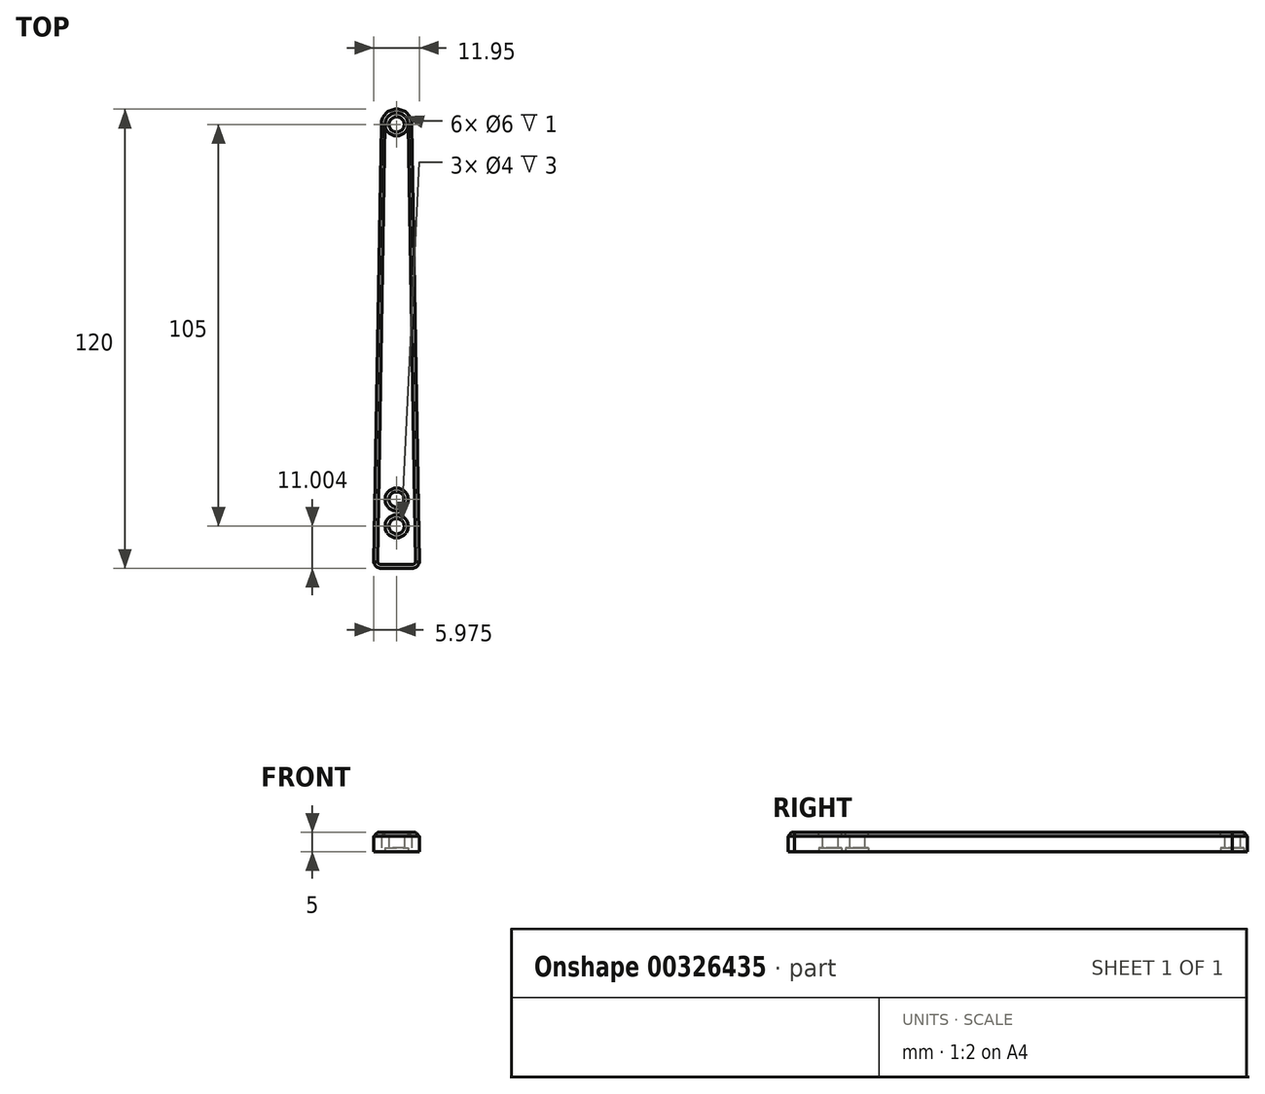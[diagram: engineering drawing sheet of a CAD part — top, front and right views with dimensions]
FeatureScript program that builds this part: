
annotation { "Feature Type Name" : "Feature", "Feature Type Description" : "" }
export const myFeature = defineFeature(function(context is Context, id is Id, definition is map)
    precondition{}
    {
        {
            var Q0;
            Q0=qCreatedBy(makeId("Top.planeOp"),FACE);
            var sketch = newSketch(context, id + "F0", { "sketchPlane" : qUnion([Q0])});
            skLineSegment(sketch, "E0.top", {"start": v(-57.1, -56.14) * mm, "end": v(-49.1, -56.14) * mm});
            skPoint(sketch, "E1", {"position": v(-53.1, 59.86) * mm});
            skArc(sketch, "E2", {"start": v(-49.1, 59.86) * mm, "mid": v(-53.1, 63.86) * mm, "end": v(-57.1, 59.86) * mm});
            skPoint(sketch, "E3.orphan", {"position": v(-57.1, 63.86) * mm});
            skPoint(sketch, "E0.bottom.end.orphan", {"position": v(-49.1, 63.86) * mm});
            skLineSegment(sketch, "E4", {"start": v(-57.1, 59.86) * mm, "end": v(-57.2, 54.18) * mm});
            skLineSegment(sketch, "E5", {"start": v(-49.1, 59.86) * mm, "end": v(-49, 54.18) * mm});
            skCircle(sketch, "E6", {"center": v(-53.1, 59.86) * mm, "radius": 2 * mm});
            skLineSegment(sketch, "E7", {"start": v(-53.1, 63.86) * mm, "end": v(-53.1, -56.14) * mm, "construction": true});
            skPoint(sketch, "E8", {"position": v(-53.1, -31.14) * mm});
            skPoint(sketch, "E9", {"position": v(-53.1, -36.14) * mm});
            skPoint(sketch, "E10", {"position": v(-53.1, -38.14) * mm});
            skPoint(sketch, "E11", {"position": v(-53.1, -45.14) * mm});
            skCircle(sketch, "E12", {"center": v(-53.1, -38.14) * mm, "radius": 2 * mm});
            skCircle(sketch, "E13", {"center": v(-53.1, -45.14) * mm, "radius": 2 * mm});
            skArc(sketch, "E14", {"start": v(-57.1, -56.14) * mm, "mid": v(-58.38, -55.66) * mm, "end": v(-59.07, -54.47) * mm});
            skArc(sketch, "E15", {"start": v(-49.1, -56.14) * mm, "mid": v(-47.8, -55.66) * mm, "end": v(-47.12, -54.47) * mm});
            skPoint(sketch, "E16.trimOffspring.end.orphan", {"position": v(-59.1, -56.14) * mm});
            skPoint(sketch, "E17.orphan", {"position": v(-47.1, -56.14) * mm});
            skLineSegment(sketch, "E18.trimOffspring", {"start": v(-57.29, 48.76) * mm, "end": v(-59.07, -54.47) * mm});
            skLineSegment(sketch, "E19.trimOffspring", {"start": v(-48.9, 48.76) * mm, "end": v(-47.12, -54.47) * mm});
            skLineSegment(sketch, "E20", {"start": v(-57.2, 54.18) * mm, "end": v(-57.22, 52.52) * mm});
            skLineSegment(sketch, "E21", {"start": v(-49, 54.18) * mm, "end": v(-48.97, 52.52) * mm});
            skLineSegment(sketch, "E22", {"start": v(-57.27, 49.52) * mm, "end": v(-57.29, 48.76) * mm});
            skLineSegment(sketch, "E23.trimOffspring", {"start": v(-48.92, 49.52) * mm, "end": v(-48.9, 48.76) * mm});
            skLineSegment(sketch, "E24", {"start": v(-48.97, 52.52) * mm, "end": v(-48.92, 49.52) * mm});
            skLineSegment(sketch, "E25", {"start": v(-57.22, 52.52) * mm, "end": v(-57.27, 49.52) * mm});
            skSolve(sketch);
        }
        {
            var Q0;
            Q0=makeQuery(id+"F0.imprint","IMPRINT",FACE,{"disambiguationData":[TD([[makeQuery(id+"F0.imprint","IMPRINT",EDGE,{"derivedFrom":sQuery(id+"F0.wireOp",EDGE,"E0.top")}),1.0]])]});
            extrude(context, id + "F1", {"entities" : qUnion([Q0]), "depth" : 5 * mm});
        }
        {
            var Q0;
            Q0=makeQuery(id+"F1.opExtrude","CAP_EDGE",EDGE,{"disambiguationData":[OSD([sQuery(id+"F0.wireOp",EDGE,"E19.trimOffspring"),sQuery(id+"F0.wireOp",EDGE,"E23.trimOffspring")])],"isStart":false});
            var Q1;
            Q1=makeQuery(id+"F1.opExtrude","CAP_EDGE",EDGE,{"disambiguationData":[OSD([sQuery(id+"F0.wireOp",EDGE,"E18.trimOffspring"),sQuery(id+"F0.wireOp",EDGE,"E22")])],"isStart":false});
            var Q2;
            Q2=makeQuery(id+"F1.opExtrude","CAP_EDGE",EDGE,{"disambiguationData":[OSD([sQuery(id+"F0.wireOp",EDGE,"E14")])],"isStart":false});
            var Q3;
            Q3=makeQuery(id+"F1.opExtrude","CAP_EDGE",EDGE,{"disambiguationData":[OSD([sQuery(id+"F0.wireOp",EDGE,"E0.top")])],"isStart":false});
            var Q4;
            Q4=makeQuery(id+"F1.opExtrude","CAP_EDGE",EDGE,{"disambiguationData":[OSD([sQuery(id+"F0.wireOp",EDGE,"E15")])],"isStart":false});
            var Q5;
            Q5=makeQuery(id+"F1.opExtrude","CAP_EDGE",EDGE,{"disambiguationData":[OSD([sQuery(id+"F0.wireOp",EDGE,"E2")])],"isStart":false});
            var Q6;
            Q6=makeQuery(id+"F1.opExtrude","CAP_EDGE",EDGE,{"disambiguationData":[OSD([sQuery(id+"F0.wireOp",EDGE,"E4"),sQuery(id+"F0.wireOp",EDGE,"E20")])],"isStart":false});
            var Q7;
            Q7=makeQuery(id+"F1.opExtrude","CAP_EDGE",EDGE,{"disambiguationData":[OSD([sQuery(id+"F0.wireOp",EDGE,"E5"),sQuery(id+"F0.wireOp",EDGE,"E21")])],"isStart":false});
            var Q8;
            Q8=makeQuery(id+"F1.opExtrude","CAP_EDGE",EDGE,{"disambiguationData":[OSD([sQuery(id+"F0.wireOp",EDGE,"o0RNKsEq-p2mH-4jjP-SO0A-SJ8OjA0UEUDv")])],"isStart":false});
            var Q9;
            Q9=makeQuery(id+"F1.opExtrude","CAP_EDGE",EDGE,{"disambiguationData":[OSD([sQuery(id+"F0.wireOp",EDGE,"rJI7la13-ssud-MAWH-iN3m-8SUHMPCMIT3g")])],"isStart":false});
            chamfer(context, id + "F2", {"entities" : qUnion([Q0, Q1, Q2, Q3, Q4, Q5, Q6, Q7, Q8, Q9]), "width" : 1 * mm, "tangentPropagation" : true});
        }
        {
            var Q0;
            Q0=makeQuery(id+"F1.opExtrude","CAP_FACE",FACE,{"disambiguationData":[OSD([sQuery(id+"F0.wireOp",EDGE,"E0.top"),sQuery(id+"F0.wireOp",EDGE,"E2"),sQuery(id+"F0.wireOp",EDGE,"E4"),sQuery(id+"F0.wireOp",EDGE,"E5"),sQuery(id+"F0.wireOp",EDGE,"E6"),sQuery(id+"F0.wireOp",EDGE,"E12"),sQuery(id+"F0.wireOp",EDGE,"E13"),sQuery(id+"F0.wireOp",EDGE,"E14"),sQuery(id+"F0.wireOp",EDGE,"E15")])],"isStart":true});
            var sketch = newSketch(context, id + "F3", { "sketchPlane" : qUnion([Q0])});
            skPoint(sketch, "E26", {"position": v(-53.1, -59.86) * mm});
            skPoint(sketch, "E27", {"position": v(-53.1, 38.14) * mm});
            skCircle(sketch, "E28", {"center": v(-53.1, 38.14) * mm, "radius": 3 * mm});
            skCircle(sketch, "E29", {"center": v(-53.1, -59.86) * mm, "radius": 3 * mm});
            skCircle(sketch, "E30", {"center": v(-53.1, 45.14) * mm, "radius": 3 * mm});
            skSolve(sketch);
        }
        {
            var Q0;
            Q0=makeQuery(id+"F3.imprint","IMPRINT",FACE,{"disambiguationData":[TD([[makeQuery(id+"F3.imprint","IMPRINT",EDGE,{"derivedFrom":sQuery(id+"F3.wireOp",EDGE,"E28")}),1.0]])]});
            var Q1;
            Q1=sQuery(id+"F3.wireOp",EDGE,"E28");
            var Q2;
            Q2=sQuery(id+"F3.wireOp",EDGE,"NuHG6ebw-mJRD-JW6i-FIXQ-FZVYiqWoZk1F");
            extrude(context, id + "F4", {"entities" : qUnion([Q0]), "operationType" : NewBodyOperationType.REMOVE, "surfaceEntities" : qUnion([Q1, Q2]), "oppositeDirection" : true, "depth" : 1 * mm});
        }
        {
            var Q0;
            Q0=makeQuery(id+"F1.opExtrude","CAP_FACE",FACE,{"disambiguationData":[OSD([sQuery(id+"F0.wireOp",EDGE,"E0.top"),sQuery(id+"F0.wireOp",EDGE,"E2"),sQuery(id+"F0.wireOp",EDGE,"E4"),sQuery(id+"F0.wireOp",EDGE,"E5"),sQuery(id+"F0.wireOp",EDGE,"E6"),sQuery(id+"F0.wireOp",EDGE,"E12"),sQuery(id+"F0.wireOp",EDGE,"E13"),sQuery(id+"F0.wireOp",EDGE,"E14"),sQuery(id+"F0.wireOp",EDGE,"E15")])],"isStart":false});
            var sketch = newSketch(context, id + "F5", { "sketchPlane" : qUnion([Q0])});
            skPoint(sketch, "E31", {"position": v(-53.1, 59.86) * mm});
            skPoint(sketch, "E32", {"position": v(-53.1, -38.14) * mm});
            skPoint(sketch, "E33", {"position": v(-53.1, -45.14) * mm});
            skCircle(sketch, "E34", {"center": v(-53.1, -38.14) * mm, "radius": 3 * mm});
            skCircle(sketch, "E35", {"center": v(-53.1, -45.14) * mm, "radius": 3 * mm});
            skCircle(sketch, "E36", {"center": v(-53.1, 59.86) * mm, "radius": 3 * mm});
            skSolve(sketch);
        }
        {
            var Q0;
            Q0=makeQuery(id+"F5.imprint","IMPRINT",FACE,{"disambiguationData":[TD([[makeQuery(id+"F5.imprint","IMPRINT",EDGE,{"derivedFrom":sQuery(id+"F5.wireOp",EDGE,"E35")}),1.0]])]});
            var Q1;
            Q1=makeQuery(id+"F5.imprint","IMPRINT",FACE,{"disambiguationData":[TD([[makeQuery(id+"F5.imprint","IMPRINT",EDGE,{"derivedFrom":sQuery(id+"F5.wireOp",EDGE,"E34")}),1.0]])]});
            var Q2;
            {var subQ1=sQuery(id+"F0.wireOp",EDGE,"E6");Q2=makeQuery(id+"F5.imprint","IMPRINT",FACE,{"disambiguationData":[TD([[makeQuery(id+"F5.imprint","IMPRINT",EDGE,{"derivedFrom":makeQuery(id+"F1.opExtrude","CAP_EDGE",EDGE,{"disambiguationData":[OSD([subQ1])],"isStart":false})}),-1.0]])]});}
            var Q3;
            Q3=sQuery(id+"F5.wireOp",EDGE,"E34");
            var Q4;
            Q4=sQuery(id+"F5.wireOp",EDGE,"E35");
            var Q5;
            Q5=sQuery(id+"F5.wireOp",EDGE,"d6FoRQbe-lIdU-fJoR-s3iu-PYYhAoR2MkCE");
            extrude(context, id + "F6", {"entities" : qUnion([Q0, Q1, Q2]), "operationType" : NewBodyOperationType.REMOVE, "surfaceEntities" : qUnion([Q3, Q4, Q5]), "oppositeDirection" : true, "depth" : 1 * mm});
        }
        {
            var Q0;
            {var subQ1=sQuery(id+"F0.wireOp",EDGE,"E6");Q0=makeQuery(id+"F3.imprint","IMPRINT",FACE,{"disambiguationData":[TD([[makeQuery(id+"F3.imprint","IMPRINT",EDGE,{"derivedFrom":makeQuery(id+"F1.opExtrude","CAP_EDGE",EDGE,{"disambiguationData":[OSD([subQ1])],"isStart":true})}),1.0]])]});}
            var Q1;
            Q1=makeQuery(id+"F3.imprint","IMPRINT",FACE,{"disambiguationData":[TD([[makeQuery(id+"F3.imprint","IMPRINT",EDGE,{"derivedFrom":sQuery(id+"F3.wireOp",EDGE,"E30")}),1.0]])]});
            extrude(context, id + "F7", {"entities" : qUnion([Q0, Q1]), "operationType" : NewBodyOperationType.REMOVE, "oppositeDirection" : true, "depth" : 1 * mm});
        }
    });
